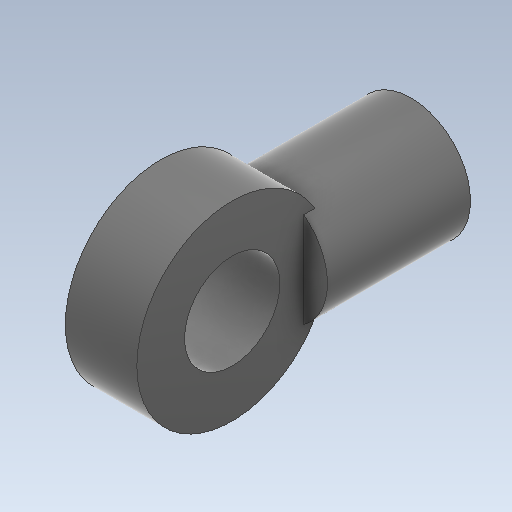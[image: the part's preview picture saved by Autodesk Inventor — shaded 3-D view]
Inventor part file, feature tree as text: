
AUTODESK INVENTOR PART (.ipt)
format: ipt  version: 2020 (Build 240168000, 168)  size: 139,264 bytes
history: native  units: mm
features: extrude x3, sketch x3, projected_geometry x2, other x1
ambient origin geometry x8: Origin, YZ Plane, XZ Plane, XY Plane, X Axis, Y Axis, Z Axis, Center Point
bodies: Body1 (feature_tree)
feature tree (9):
  other  "ソリッド1"
  extrude  "押し出し1"  Depth=5.0mm
  sketch  "スケッチ2"
  extrude  "押し出し2"  Depth=5.0mm TaperAngle=0.0deg
  extrude  "押し出し3"  Depth=4.0mm
  sketch  "スケッチ1"
  projected_geometry  "投影ループ1"
  sketch  "スケッチ3"
  projected_geometry  "投影ループ2"
